# Revit family: Sink-Bradley_Corp-Verge-LVLD3
name_source: partatom
category: Plumbing Fixtures
revit_build: Autodesk Revit Architecture 2012 (Build: 20110916_2132(x64)
units: mm (PartAtom-declared; Revit-internal decimal feet)

## types (2) — shared parameters
ADA Compliant = Yes
Apparent Load = 0 VA
Assembly Code = D2010400
Bottom_of_Trap_Cover = 14.5 "
Bowl_Edge_Under_Faucet = No
Bowl_Edge_Under_Soap_Dispenser = No
Buy American Act = To Be Determined
Cold_Supply_L/R = 10.5 "
Depth = 19.5 "
Description = Verge® Lavatory System - LVLD-Series, Three-Station
Drain_Height = 7.75 "
Drain_L/R = 1.75 "
Electrical_C = 1 "
Electrical_Height = 7 "
Electrical_L = 30.375 "
Electrical_R = 30.375 "
Faucet = Yes
Faucet Material = Chrome
Frequency = 0 Hz
Height = 20 "
Hot_Supply_L/R = 7.5 "
Industry Standards = TAS, ICC A117.1 606.5, ANSI Z124.3, IGC 156, CSA B45 Series (R08), ASME A112.18.1/CSA B125.1, UPC, GREENGUARD Indoor Air Quality Certified®, GREENGUARD Children & Schools(SM)
Installation Type = Wall Mounted
Low Emitting Material = Yes
Manufacturer = Bradley Corporation
MasterFormat Number = 22 42 16
MasterFormat Title = Commercial Lavatories and Sinks
Material = Polyester Resin
Material Note = Other Evero™ colors available - See www.bradleycorp.com
Model = LVLD3
NO = No
Number of Poles = 1
OmniClass Table 21 Number = 21-04 20 10 60
OmniClass Table 21 Title = Plumbing Fixtures
OmniClass Table 23 Number = 23-31 13 00
OmniClass Table 23 Title = Sinks/Lavatories
Product Tech Data URL - English = http://bradleycorp.com
Soap Dispenser = Yes
Soap Dispenser Material = Chrome
Specifications URL = http://www.bradleycorp.com
Strainer Material = Stainless Steel
Strainer_Under_Faucet = No
Supply_Height = 13 "
Trap Cover Material = Stainless Steel
Type Comments = Verge® Lavatory System - LVLD-Series
URL = http://www.bradleycorp.com
Version = 2.0
Voltage = 110 V
Warranty Information = Evero material warranted for fifteen years. All other components warranted for one year.
Width = 90 "
YES = Yes
zero-valued in all types: Percentage of Recycled Content, Power Factor

## per-type parameters (varying)
| type | Top_of_Deck_Height |
| ADA Standard and TAS Height | 34.5 " |
| Juvenile and TAS, Grades 6 - 12 | 31.5 " |

## geometry (parser evidence)
native form markers: Blend x18, Sweep x7
no freeform markers — native parametric forms only
